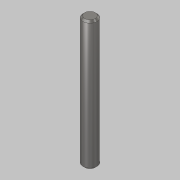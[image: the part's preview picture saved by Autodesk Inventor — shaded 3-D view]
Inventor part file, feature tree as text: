
AUTODESK INVENTOR PART (.ipt)
format: ipt  version: 2019.2 (Build 232265000, 265)  size: 78,336 bytes
history: native  units: mm
features: other x1, extrude x1, chamfer x1, sketch x1
ambient origin geometry x8: Origin, YZ Plane, XZ Plane, XY Plane, X Axis, Y Axis, Z Axis, Center Point
bodies: Volumenkörper1 (feature_tree)
feature tree (4):
  other  "Shaft1.ipt"
  extrude  "Extrusion1"  Depth=18.5mm TaperAngle=0.0deg
  chamfer  "Fase1"  Distance=0.25mm Angle=45.0deg
  sketch  "Skizze1"  dims[d0=10.0mm d1=18.5mm d2=0.0mm d3=0.25mm d4=2.0mm d5=45.0deg]
